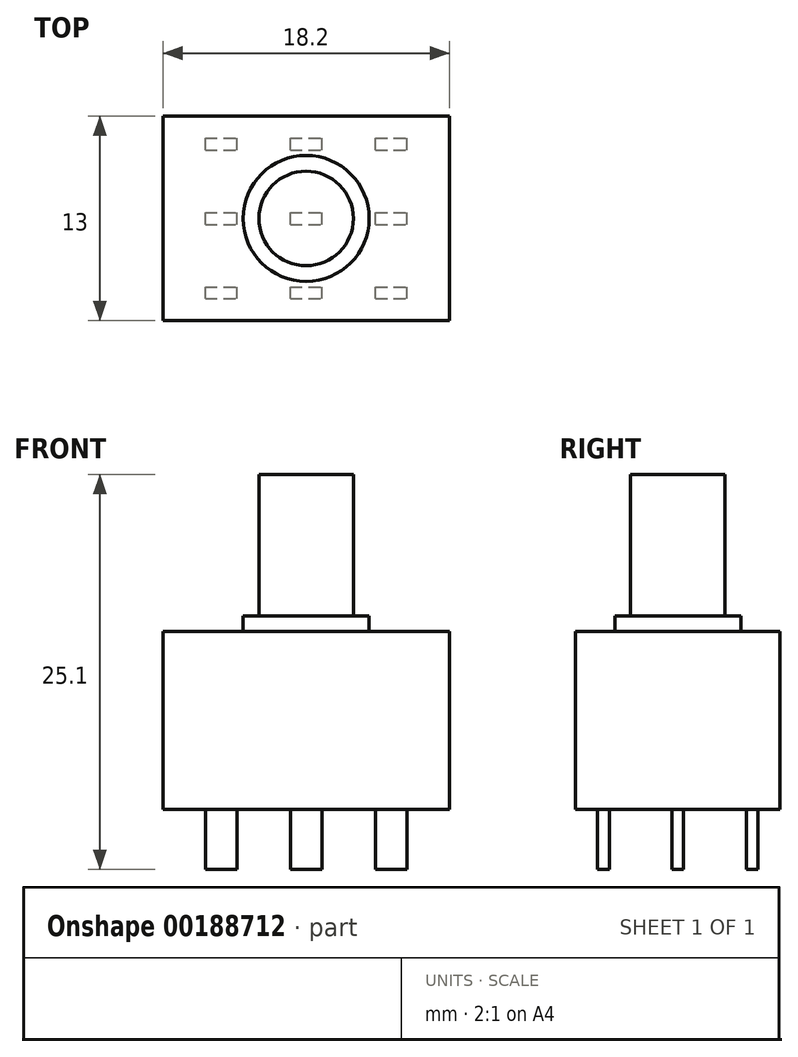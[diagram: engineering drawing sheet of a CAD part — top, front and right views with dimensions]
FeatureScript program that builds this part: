
annotation { "Feature Type Name" : "Feature", "Feature Type Description" : "" }
export const myFeature = defineFeature(function(context is Context, id is Id, definition is map)
    precondition{}
    {
        {
            var Q0;
            Q0=qCreatedBy(makeId("Top.planeOp"),FACE);
            var sketch = newSketch(context, id + "F0", { "sketchPlane" : qUnion([Q0])});
            skLineSegment(sketch, "E0.bottom", {"start": v(9.1, -6.5) * mm, "end": v(-9.1, -6.5) * mm});
            skLineSegment(sketch, "E0.top", {"start": v(9.1, 6.5) * mm, "end": v(-9.1, 6.5) * mm});
            skLineSegment(sketch, "E0.left", {"start": v(9.1, -6.5) * mm, "end": v(9.1, 6.5) * mm});
            skLineSegment(sketch, "E0.right", {"start": v(-9.1, -6.5) * mm, "end": v(-9.1, 6.5) * mm});
            skPoint(sketch, "E0.middle", {"position": v(0, 0) * mm});
            skSolve(sketch);
        }
        {
            var Q0;
            Q0=makeQuery(id+"F0.imprint","IMPRINT",FACE,{"disambiguationData":[TD([[makeQuery(id+"F0.imprint","IMPRINT",EDGE,{"derivedFrom":sQuery(id+"F0.wireOp",EDGE,"E0.bottom")}),-1.0]])]});
            extrude(context, id + "F1", {"entities" : qUnion([Q0]), "depth" : 11.3 * mm, "offsetDistance" : 25 * mm});
        }
        {
            var Q0;
            Q0=makeQuery(id+"F1.opExtrude","CAP_FACE",FACE,{"disambiguationData":[OSD([sQuery(id+"F0.wireOp",EDGE,"E0.bottom"),sQuery(id+"F0.wireOp",EDGE,"E0.top"),sQuery(id+"F0.wireOp",EDGE,"E0.left"),sQuery(id+"F0.wireOp",EDGE,"E0.right")])],"isStart":false});
            var sketch = newSketch(context, id + "F2", { "sketchPlane" : qUnion([Q0])});
            skCircle(sketch, "E1", {"center": v(0, 0) * mm, "radius": 4 * mm});
            skCircle(sketch, "E2", {"center": v(0, 0) * mm, "radius": 3 * mm});
            skSolve(sketch);
        }
        {
            var Q0;
            Q0=makeQuery(id+"F2.imprint","IMPRINT",FACE,{"disambiguationData":[TD([[makeQuery(id+"F2.imprint","IMPRINT",EDGE,{"derivedFrom":sQuery(id+"F2.wireOp",EDGE,"E1")}),1.0]])]});
            extrude(context, id + "F3", {"entities" : qUnion([Q0]), "operationType" : NewBodyOperationType.ADD, "depth" : 1 * mm, "offsetDistance" : 25 * mm});
        }
        {
            var Q0;
            Q0=makeQuery(id+"F3.boolean.opBoolean","SPLIT",FACE,{"disambiguationData":[TD([makeQuery(id+"F3.opExtrude","SWEPT_FACE",FACE,{"disambiguationData":[OSD([sQuery(id+"F2.wireOp",EDGE,"E2")])]})])],"derivedFrom":makeQuery(id+"F1.opExtrude","CAP_FACE",FACE,{"disambiguationData":[OSD([sQuery(id+"F0.wireOp",EDGE,"E0.bottom"),sQuery(id+"F0.wireOp",EDGE,"E0.top"),sQuery(id+"F0.wireOp",EDGE,"E0.left"),sQuery(id+"F0.wireOp",EDGE,"E0.right")])],"isStart":false})});
            extrude(context, id + "F4", {"entities" : qUnion([Q0]), "operationType" : NewBodyOperationType.ADD, "depth" : 10 * mm, "offsetDistance" : 25 * mm});
        }
        {
            var Q0;
            Q0=makeQuery(id+"F1.opExtrude","CAP_FACE",FACE,{"disambiguationData":[OSD([sQuery(id+"F0.wireOp",EDGE,"E0.bottom"),sQuery(id+"F0.wireOp",EDGE,"E0.top"),sQuery(id+"F0.wireOp",EDGE,"E0.left"),sQuery(id+"F0.wireOp",EDGE,"E0.right")])],"isStart":true});
            var sketch = newSketch(context, id + "F5", { "sketchPlane" : qUnion([Q0])});
            skLineSegment(sketch, "E3.bottom", {"start": v(-6.4, 5.1) * mm, "end": v(-4.4, 5.1) * mm});
            skLineSegment(sketch, "E3.top", {"start": v(-6.4, 4.35) * mm, "end": v(-4.4, 4.35) * mm});
            skLineSegment(sketch, "E3.left", {"start": v(-6.4, 5.1) * mm, "end": v(-6.4, 4.35) * mm});
            skLineSegment(sketch, "E3.right", {"start": v(-4.4, 5.1) * mm, "end": v(-4.4, 4.35) * mm});
            skLineSegment(sketch, "E4", {"start": v(-9.1, 0) * mm, "end": v(9.1, 0) * mm, "construction": true});
            skLineSegment(sketch, "E5", {"start": v(0, 6.5) * mm, "end": v(0, -6.5) * mm, "construction": true});
            skLineSegment(sketch, "E6.1.0.0", {"start": v(-1, 4.35) * mm, "end": v(1, 4.35) * mm});
            skLineSegment(sketch, "E6.1.0.1", {"start": v(1, 5.1) * mm, "end": v(1, 4.35) * mm});
            skLineSegment(sketch, "E6.1.0.2", {"start": v(-1, 5.1) * mm, "end": v(-1, 4.35) * mm});
            skLineSegment(sketch, "E6.1.0.3", {"start": v(-1, 5.1) * mm, "end": v(1, 5.1) * mm});
            skLineSegment(sketch, "E6.2.0.0", {"start": v(4.4, 4.35) * mm, "end": v(6.4, 4.35) * mm});
            skLineSegment(sketch, "E6.2.0.1", {"start": v(6.4, 5.1) * mm, "end": v(6.4, 4.35) * mm});
            skLineSegment(sketch, "E6.2.0.2", {"start": v(4.4, 5.1) * mm, "end": v(4.4, 4.35) * mm});
            skLineSegment(sketch, "E6.2.0.3", {"start": v(4.4, 5.1) * mm, "end": v(6.4, 5.1) * mm});
            skLineSegment(sketch, "E6.direction1", {"start": v(-6.4, 4.35) * mm, "end": v(-1, 4.35) * mm, "construction": true});
            skLineSegment(sketch, "E7.1.0.0", {"start": v(-6.4, -0.38) * mm, "end": v(-1, -0.38) * mm, "construction": true});
            skLineSegment(sketch, "E7.1.0.1", {"start": v(4.4, 0.37) * mm, "end": v(6.4, 0.37) * mm});
            skLineSegment(sketch, "E7.1.0.2", {"start": v(4.4, -0.38) * mm, "end": v(6.4, -0.38) * mm});
            skLineSegment(sketch, "E7.1.0.3", {"start": v(-1, -0.38) * mm, "end": v(1, -0.38) * mm});
            skLineSegment(sketch, "E7.1.0.4", {"start": v(-1, 0.37) * mm, "end": v(1, 0.37) * mm});
            skLineSegment(sketch, "E7.1.0.5", {"start": v(-6.4, 0.37) * mm, "end": v(-4.4, 0.37) * mm});
            skLineSegment(sketch, "E7.1.0.6", {"start": v(-6.4, -0.38) * mm, "end": v(-4.4, -0.38) * mm});
            skLineSegment(sketch, "E7.1.0.7", {"start": v(1, 0.37) * mm, "end": v(1, -0.38) * mm});
            skLineSegment(sketch, "E7.1.0.8", {"start": v(-6.4, 0.37) * mm, "end": v(-6.4, -0.38) * mm});
            skLineSegment(sketch, "E7.1.0.9", {"start": v(-1, 0.37) * mm, "end": v(-1, -0.38) * mm});
            skLineSegment(sketch, "E7.1.0.10", {"start": v(6.4, 0.37) * mm, "end": v(6.4, -0.38) * mm});
            skLineSegment(sketch, "E7.1.0.11", {"start": v(-4.4, 0.37) * mm, "end": v(-4.4, -0.38) * mm});
            skLineSegment(sketch, "E7.1.0.12", {"start": v(4.4, 0.37) * mm, "end": v(4.4, -0.38) * mm});
            skLineSegment(sketch, "E7.2.0.0", {"start": v(-6.4, -5.1) * mm, "end": v(-1, -5.1) * mm, "construction": true});
            skLineSegment(sketch, "E7.2.0.1", {"start": v(4.4, -4.35) * mm, "end": v(6.4, -4.35) * mm});
            skLineSegment(sketch, "E7.2.0.2", {"start": v(4.4, -5.1) * mm, "end": v(6.4, -5.1) * mm});
            skLineSegment(sketch, "E7.2.0.3", {"start": v(-1, -5.1) * mm, "end": v(1, -5.1) * mm});
            skLineSegment(sketch, "E7.2.0.4", {"start": v(-1, -4.35) * mm, "end": v(1, -4.35) * mm});
            skLineSegment(sketch, "E7.2.0.5", {"start": v(-6.4, -4.35) * mm, "end": v(-4.4, -4.35) * mm});
            skLineSegment(sketch, "E7.2.0.6", {"start": v(-6.4, -5.1) * mm, "end": v(-4.4, -5.1) * mm});
            skLineSegment(sketch, "E7.2.0.7", {"start": v(1, -4.35) * mm, "end": v(1, -5.1) * mm});
            skLineSegment(sketch, "E7.2.0.8", {"start": v(-6.4, -4.35) * mm, "end": v(-6.4, -5.1) * mm});
            skLineSegment(sketch, "E7.2.0.9", {"start": v(-1, -4.35) * mm, "end": v(-1, -5.1) * mm});
            skLineSegment(sketch, "E7.2.0.10", {"start": v(6.4, -4.35) * mm, "end": v(6.4, -5.1) * mm});
            skLineSegment(sketch, "E7.2.0.11", {"start": v(-4.4, -4.35) * mm, "end": v(-4.4, -5.1) * mm});
            skLineSegment(sketch, "E7.2.0.12", {"start": v(4.4, -4.35) * mm, "end": v(4.4, -5.1) * mm});
            skLineSegment(sketch, "E7.direction1", {"start": v(-6.4, 4.35) * mm, "end": v(-6.4, -0.38) * mm, "construction": true});
            skSolve(sketch);
        }
        {
            var Q0;
            Q0 = qSketchRegion(id + "F5", true);
            extrude(context, id + "F6", {"entities" : qUnion([Q0]), "operationType" : NewBodyOperationType.ADD, "depth" : 3.8 * mm, "offsetDistance" : 25 * mm});
        }
    });
